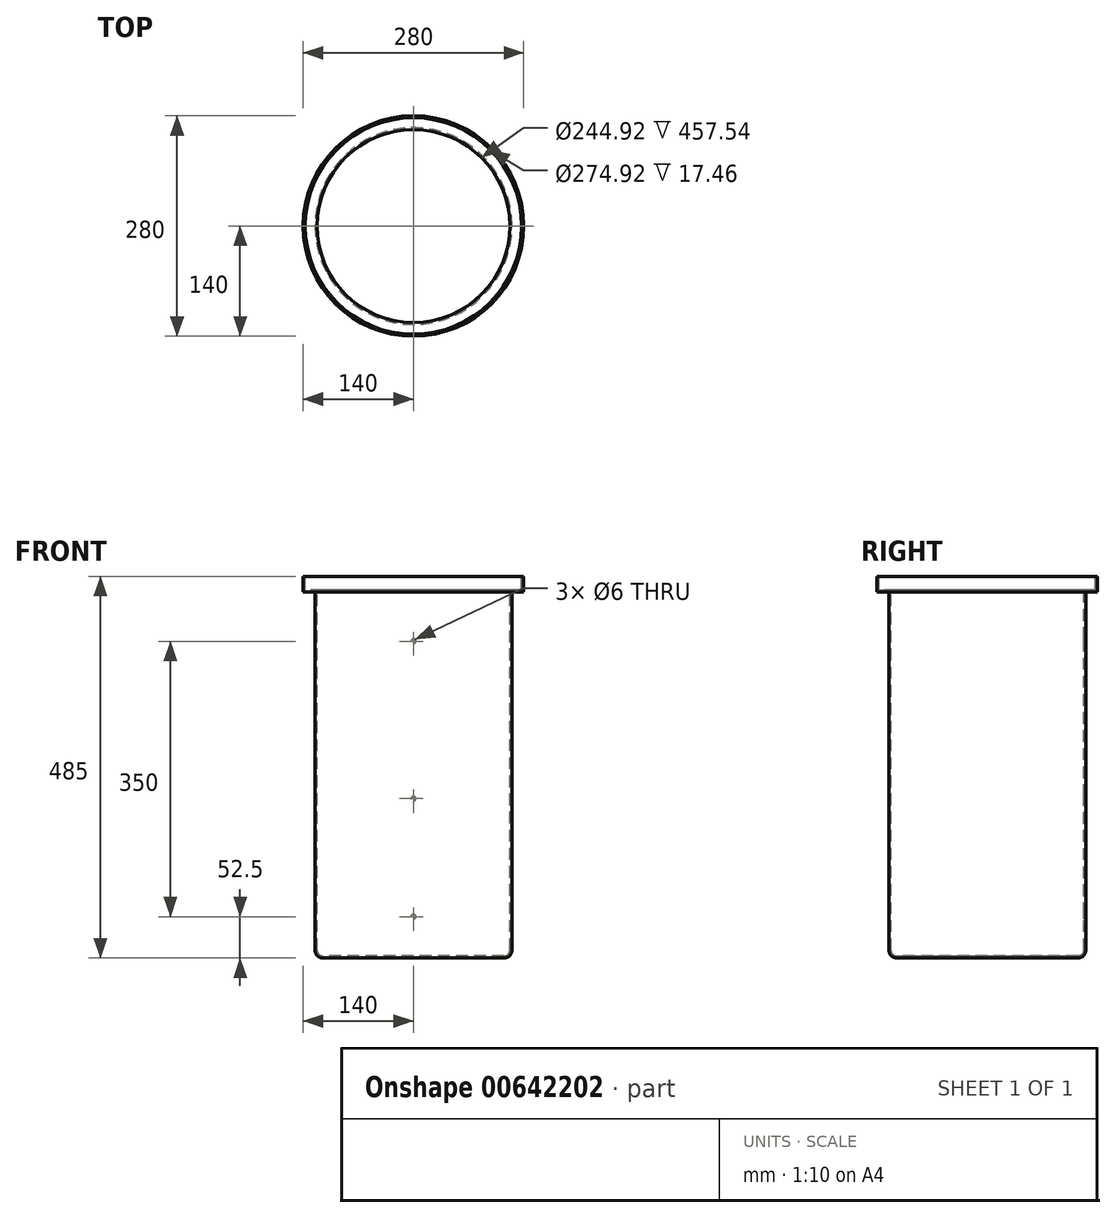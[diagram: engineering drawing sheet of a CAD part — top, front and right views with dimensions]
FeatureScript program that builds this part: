
annotation { "Feature Type Name" : "Feature", "Feature Type Description" : "" }
export const myFeature = defineFeature(function(context is Context, id is Id, definition is map)
    precondition{}
    {
        {
            var Q0;
            Q0=qCreatedBy(makeId("Front.planeOp"),FACE);
            var sketch = newSketch(context, id + "F0", { "sketchPlane" : qUnion([Q0])});
            skLineSegment(sketch, "E0", {"start": v(0, -242.5) * mm, "end": v(115, -242.5) * mm});
            skLineSegment(sketch, "E1", {"start": v(125, -232.5) * mm, "end": v(125, 222.5) * mm});
            skLineSegment(sketch, "E2", {"start": v(125, 222.5) * mm, "end": v(140, 222.5) * mm});
            skLineSegment(sketch, "E3", {"start": v(140, 222.5) * mm, "end": v(140, 242.5) * mm});
            skLineSegment(sketch, "E4", {"start": v(140, 242.5) * mm, "end": v(0, 242.5) * mm});
            skLineSegment(sketch, "E5", {"start": v(0, 242.5) * mm, "end": v(0, -242.5) * mm});
            skPoint(sketch, "E6.visualSharp", {"position": v(125, -242.5) * mm});
            skArc(sketch, "E6.filletArc", {"start": v(115, -242.5) * mm, "mid": v(122.07, -239.57) * mm, "end": v(125, -232.5) * mm});
            skSolve(sketch);
        }
        {
            var Q0;
            Q0 = qSketchRegion(id + "F0", true);
            var Q1;
            Q1=sQuery(id+"F0.wireOp",EDGE,"E5");
            revolve(context, id + "F1", {"entities" : qUnion([Q0]), "axis" : qUnion([Q1]), "revolveType" : RevolveType.FULL});
        }
        {
            var Q0;
            Q0=makeQuery(id+"F1.opRevolve","SWEPT_FACE",FACE,{"disambiguationData":[OSD([sQuery(id+"F0.wireOp",EDGE,"E4")])]});
            shell(context, id + "F2", {"entities" : qUnion([Q0]), "thickness" : 2.54 * mm});
        }
        {
            var Q0;
            Q0=qCreatedBy(makeId("Front.planeOp"),FACE);
            var sketch = newSketch(context, id + "F3", { "sketchPlane" : qUnion([Q0])});
            skCircle(sketch, "E7", {"center": v(0, 160) * mm, "radius": 3 * mm});
            skCircle(sketch, "E8", {"center": v(0, -40) * mm, "radius": 3 * mm});
            skCircle(sketch, "E9", {"center": v(0, -190) * mm, "radius": 3 * mm});
            skSolve(sketch);
        }
        {
            var Q0;
            Q0 = qSketchRegion(id + "F3", true);
            extrude(context, id + "F4", {"entities" : qUnion([Q0]), "operationType" : NewBodyOperationType.REMOVE, "endBound" : BoundingType.THROUGH_ALL, "oppositeDirection" : true, "depth" : 25 * mm, "offsetDistance" : 25 * mm});
        }
    });
